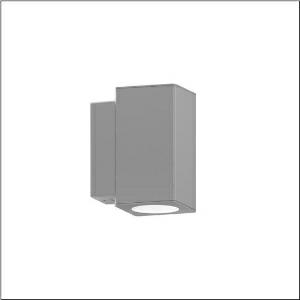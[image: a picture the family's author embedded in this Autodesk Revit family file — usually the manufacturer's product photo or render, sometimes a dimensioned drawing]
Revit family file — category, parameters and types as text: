
# Revit family: cl_31_wand_5cl553613
name_source: partatom
category: Lighting Fixtures
units: mm (PartAtom-declared; Revit-internal decimal feet)

## family parameters
Cut with Voids When Loaded = No
Host = Face
Light Source = No
Part Type = Normal
Room Calculation Point = No
Round Connector Dimension = Use Diameter
Shared = No

## types (1)
- --- (1 x LED, 300 lm, 2.8 W, 3000K)
    Apparent Load = 3 VA
    CIE Flux Codes = 98 100 100 100 100
    Color Rendering = 80
    Color Temperature = 3000K
    Default Elevation = 1800 mm
    Description = CL 31 Wall, wall luminaire, primary light control with reflector, of aluminium, primary optical cover: cover panel, of glass, transparent, light emission: down distribution, primary light characteristic: symmetric, installation type: surface-mounted, for 1x LED, rated luminous flux: 300lm, luminous efficacy: 106lm/W, light colour: 830, colour temperature: 3000K, control gear: ECG DALI, with terminal, 5-pole, max. 2.5mm², mains connection: 220..240V, AC, 50/60Hz, rated input power: 2.8W, luminaire housing, square, of aluminium, powder-coated, Siteco® metallic grey, length: 143mm, width: 100mm, height: 186mm, protection rating (complete): IP65, insulation class (complete): insulation class I (protective earthing), certification: CE, ENEC, impact resistance: IK08, permissible operating ambient temperature for outdoor applications: -20..+50°C, packaging unit: 1 piece
    Height = 186 mm
    Lamp = 1 x LED
    Lamp Light Flux = 300 lm
    Lamp Power = 2.8 W
    Lamp count = 1
    Length = 100 mm  [stored 0.328084 ft]
    Luminous efficacy = 107 lm/W
    Manufacturer = Siteco
    ModVariant = No
    Model = 5CL553613
    Mounting Place = Wall
    Mounting Type = Surface mounted
    Number of Poles = 1
    OnlyDefault = Yes
    Power Factor = 1
    Product Name = CL 31 Wand
    Product group = wall luminaire
    ProductGroupID = 2001
    Protection Class = Protection class I
    Protection Degree = IP 65
    RLX_Detail_Level = 1
    RlxData = <blob elided: 42985 chars, md5=dce7c5c1>
    Socket = socket
    Standby Power = 0 W
    System Light Flux = 300 lm
    System Power = 3 W
    Type Comments = factory setting: luminous flux: 100 % | dim-lin: 254 | 70 mA
    Type Image = l_1006895.jpg
    URL = http://relux.com
    VarID = @adj_117249
    Voltage = 0 V
    Weight = 0.00 kg
    Width = 143 mm

note: [stored X ft] marks values corroborated as IEEE doubles in the binary element streams (Revit-internal decimal feet)

## geometry (parser evidence)
native form markers: Blend x4, Sweep x11
no freeform markers — native parametric forms only
